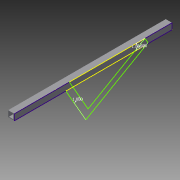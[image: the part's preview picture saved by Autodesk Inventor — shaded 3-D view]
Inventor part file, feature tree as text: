
AUTODESK INVENTOR PART (.ipt)
format: ipt  version: 2013 (Build 170138000, 138)  size: 84,480 bytes
history: native  units: in
note: dims shown in document units (in); Inventor stores cm internally (conversion verified against a paired STEP export)
features: sketch x2, extrude x1
ambient origin geometry x8: Origin, YZ Plane, XZ Plane, XY Plane, X Axis, Y Axis, Z Axis, Center Point
bodies: Solid1 (feature_tree)
feature tree (3):
  extrude  "Extrusion1"  Depth=1.0in
  sketch  "Sketch2"  dims[d3=0.125in d4=26.0in d5=0.0in d6=1.0in d9=1.0in d12=1.0in]
  sketch  "Sketch1"  dims[d0=1.0in d2=1.0in]
